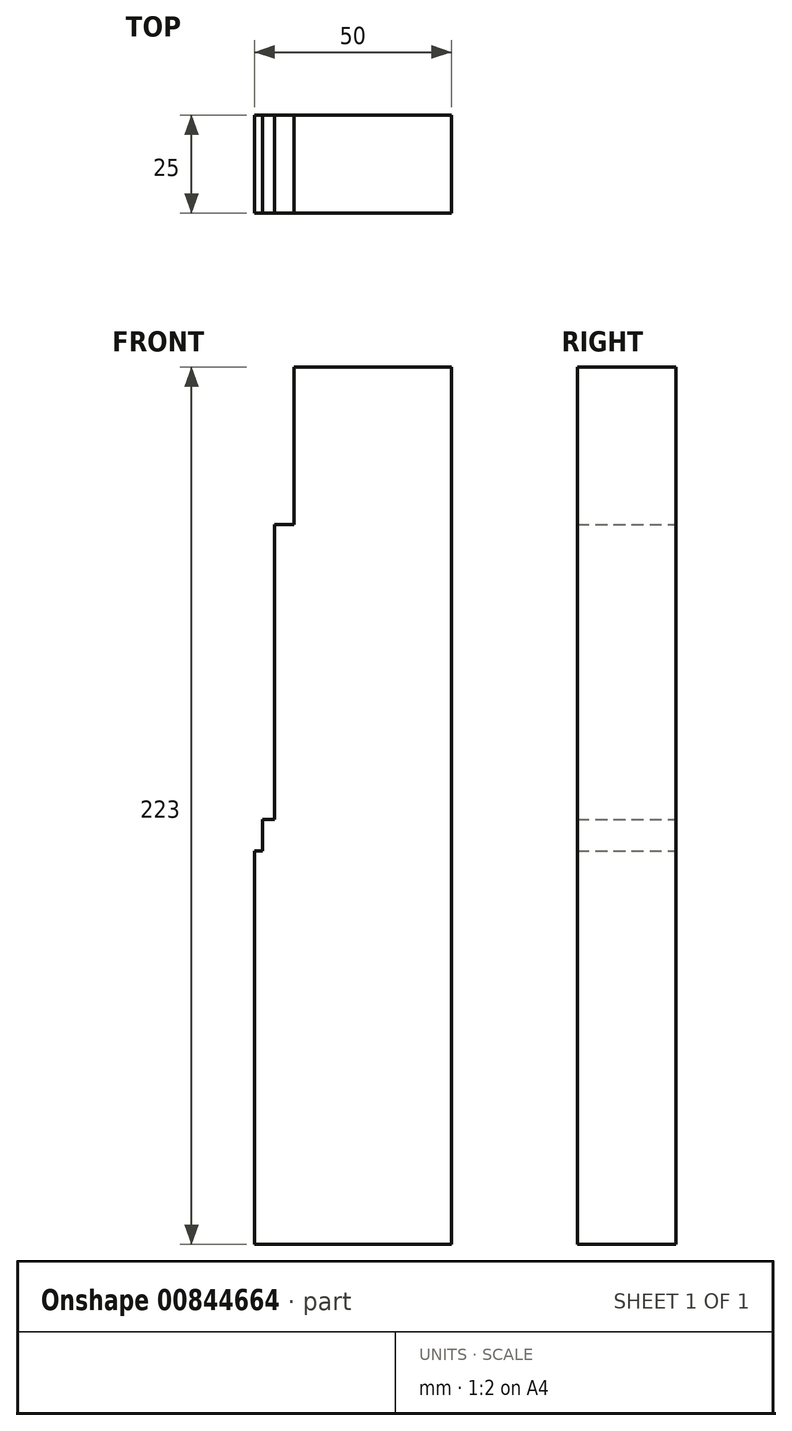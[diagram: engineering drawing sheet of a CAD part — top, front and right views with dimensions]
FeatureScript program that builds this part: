
annotation { "Feature Type Name" : "Feature", "Feature Type Description" : "" }
export const myFeature = defineFeature(function(context is Context, id is Id, definition is map)
    precondition{}
    {
        {
            var Q0;
            Q0=qCreatedBy(makeId("Front.planeOp"),FACE);
            var sketch = newSketch(context, id + "F0", { "sketchPlane" : qUnion([Q0])});
            skLineSegment(sketch, "E0.bottom", {"start": v(-45, 75) * mm, "end": v(0, 75) * mm});
            skLineSegment(sketch, "E0.top", {"start": v(-45, 0) * mm, "end": v(0, 0) * mm});
            skLineSegment(sketch, "E0.left", {"start": v(-45, 75) * mm, "end": v(-45, 0) * mm});
            skLineSegment(sketch, "E0.right", {"start": v(0, 75) * mm, "end": v(0, 0) * mm});
            skLineSegment(sketch, "E1.bottom", {"start": v(0, 0) * mm, "end": v(-48, 0) * mm});
            skLineSegment(sketch, "E1.top", {"start": v(0, -8) * mm, "end": v(-48, -8) * mm});
            skLineSegment(sketch, "E1.left", {"start": v(0, 0) * mm, "end": v(0, -8) * mm});
            skLineSegment(sketch, "E1.right", {"start": v(-48, 0) * mm, "end": v(-48, -8) * mm});
            skLineSegment(sketch, "E2.bottom", {"start": v(0, 75) * mm, "end": v(-40, 75) * mm});
            skLineSegment(sketch, "E2.top", {"start": v(0, 115) * mm, "end": v(-40, 115) * mm});
            skLineSegment(sketch, "E2.left", {"start": v(0, 75) * mm, "end": v(0, 115) * mm});
            skLineSegment(sketch, "E2.right", {"start": v(-40, 75) * mm, "end": v(-40, 115) * mm});
            skLineSegment(sketch, "E3.bottom", {"start": v(0, -8) * mm, "end": v(-50, -8) * mm});
            skLineSegment(sketch, "E3.top", {"start": v(0, -108) * mm, "end": v(-50, -108) * mm});
            skLineSegment(sketch, "E3.left", {"start": v(0, -8) * mm, "end": v(0, -108) * mm});
            skLineSegment(sketch, "E3.right", {"start": v(-50, -8) * mm, "end": v(-50, -108) * mm});
            skSolve(sketch);
        }
        {
            var Q0;
            Q0 = qSketchRegion(id + "F0", true);
            extrude(context, id + "F1", {"entities" : qUnion([Q0]), "depth" : 25 * mm, "offsetDistance" : 25 * mm});
        }
    });
